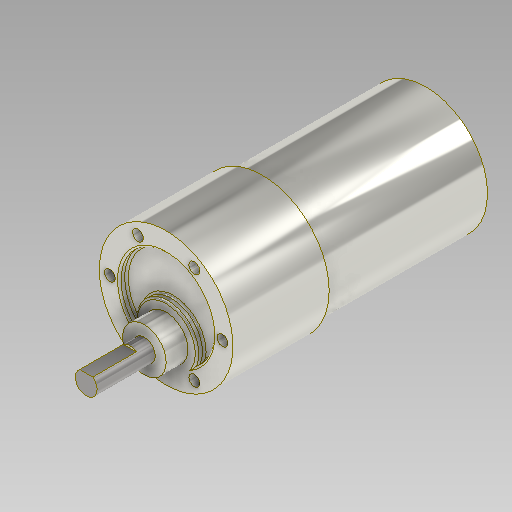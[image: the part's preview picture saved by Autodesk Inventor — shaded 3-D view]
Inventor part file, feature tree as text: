
AUTODESK INVENTOR PART (.ipt)
format: ipt  version: 2020 (Build 240168000, 168)  size: 254,464 bytes
history: native  units: mm
features: extrude x7, sketch x7, fillet x1
ambient origin geometry x8: Origin, YZ Plane, XZ Plane, XY Plane, X Axis, Y Axis, Z Axis, Center Point
bodies: Solid1 (feature_tree)
feature tree (15):
  extrude  "Extrusion1"  Depth=26.5mm TaperAngle=0.0deg
  extrude  "Extrusion2"  Depth=12.0mm
  extrude  "Extrusion3"  Depth=6.0mm
  extrude  "Extrusion4"  Depth=5.4mm
  extrude  "Extrusion5"  Depth=17.0mm
  fillet  "Fillet1"  Radius=17.0mm
  extrude  "Extrusion6"  Depth=0.5mm
  extrude  "Extrusion7"  Depth=45.0mm TaperAngle=360.0deg
  sketch  "Sketch1"  dims[d0=36.8mm d1=26.5mm d2=0.0mm]
  sketch  "Sketch2"  dims[d3=7.0mm d4=12.0mm]
  sketch  "Sketch3"  dims[d5=6.0mm d6=0.0mm d7=6.0mm]
  sketch  "Sketch4"  dims[d8=16.0mm d9=0.0mm d10=5.4mm]
  sketch  "Sketch5"  dims[d11=12.0mm d12=0.0mm d13=5.5mm d14=17.0mm]
  sketch  "Sketch6"  dims[d15=2.0mm d16=0.0mm d17=0.5mm]
  sketch  "Sketch7"  dims[d18=3.0mm d19=60.0mm d21=360.0deg d23=31.0mm d24=0.0mm d25=0.0mm d26=34.0mm d27=45.0mm d28=0.0mm d29=0.872665mm]
